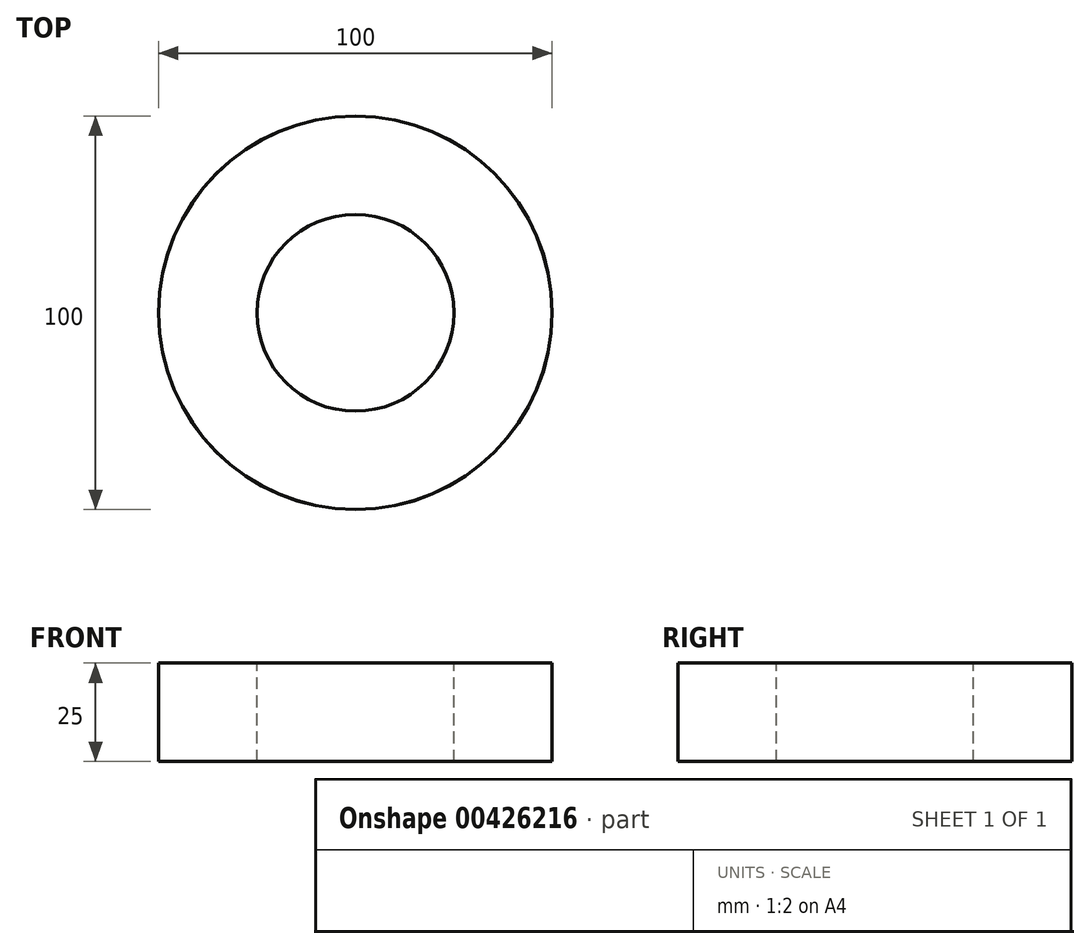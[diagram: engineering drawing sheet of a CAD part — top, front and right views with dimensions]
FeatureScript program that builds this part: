
annotation { "Feature Type Name" : "Feature", "Feature Type Description" : "" }
export const myFeature = defineFeature(function(context is Context, id is Id, definition is map)
    precondition{}
    {
        {
            var Q0;
            Q0=qCreatedBy(makeId("Top.planeOp"),FACE);
            var sketch = newSketch(context, id + "F0", { "sketchPlane" : qUnion([Q0])});
            skCircle(sketch, "E0", {"center": v(0, 0) * mm, "radius": 50 * mm});
            skCircle(sketch, "E1", {"center": v(0, 0) * mm, "radius": 25 * mm});
            skSolve(sketch);
        }
        {
            var Q0;
            Q0 = qSketchRegion(id + "F0", true);
            var Q1;
            Q1=sQuery(id+"F0.wireOp",EDGE,"E0");
            var Q2;
            Q2=sQuery(id+"F0.wireOp",EDGE,"E1");
            extrude(context, id + "F1", {"entities" : qUnion([Q0]), "bodyType" : ToolBodyType.SURFACE, "surfaceEntities" : qUnion([Q1, Q2]), "depth" : 25 * mm});
        }
        {
            var Q0;
            Q0=qCreatedBy(makeId("Top.planeOp"),FACE);
            cPlane(context, id + "F2", {"entities" : qUnion([Q0]), "cplaneType" : CPlaneType.OFFSET, "offset" : 25 * mm, "width" : 150 * mm, "height" : 150 * mm});
        }
        {
            var Q0;
            Q0=qCreatedBy(id+"F2.planeOp",FACE);
            var sketch = newSketch(context, id + "F3", { "sketchPlane" : qUnion([Q0])});
            skCircle(sketch, "E2.0", {"center": v(0, 0) * mm, "radius": 50 * mm});
            skSolve(sketch);
        }
        {
            var Q0;
            Q0=qCreatedBy(makeId("Front.planeOp"),FACE);
            var sketch = newSketch(context, id + "F4", { "sketchPlane" : qUnion([Q0])});
            skLineSegment(sketch, "E3", {"start": v(0, 0) * mm, "end": v(49.96, 0) * mm});
            skLineSegment(sketch, "E4", {"start": v(0, 0) * mm, "end": v(0, -14.35) * mm, "construction": true});
            skSolve(sketch);
        }
        {
            var Q0;
            Q0=sQuery(id+"F4.wireOp",EDGE,"E3");
            var Q1;
            Q1=sQuery(id+"F4.wireOp",EDGE,"E4");
            revolve(context, id + "F5", {"bodyType" : ToolBodyType.SURFACE, "surfaceEntities" : qUnion([Q0]), "axis" : qUnion([Q1]), "revolveType" : RevolveType.FULL});
        }
    });
